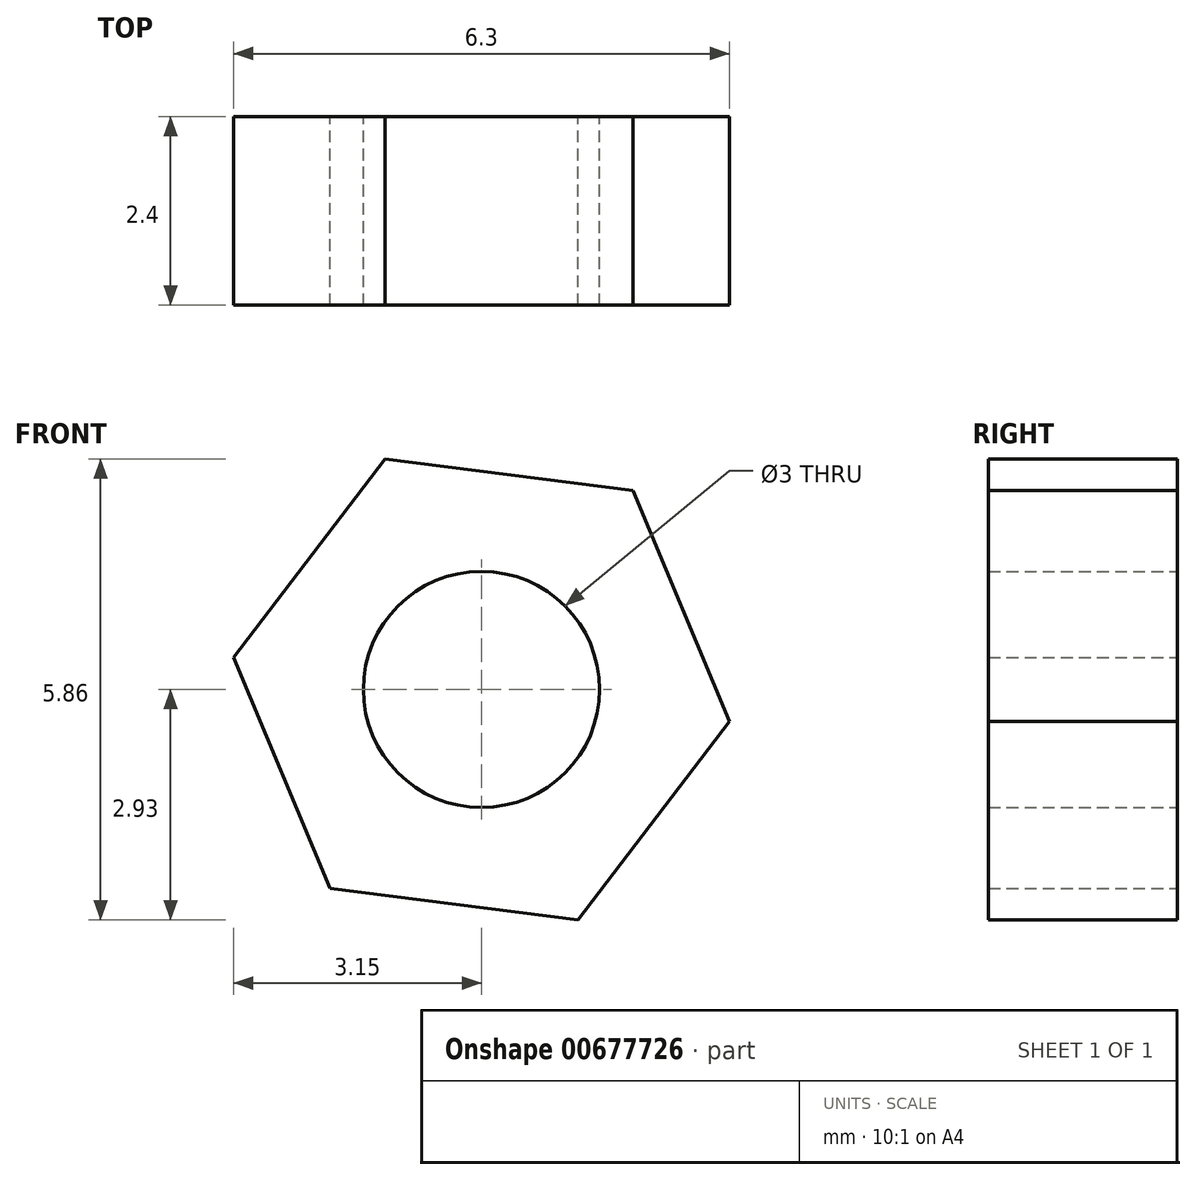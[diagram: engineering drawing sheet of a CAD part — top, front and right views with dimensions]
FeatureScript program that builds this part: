
annotation { "Feature Type Name" : "Feature", "Feature Type Description" : "" }
export const myFeature = defineFeature(function(context is Context, id is Id, definition is map)
    precondition{}
    {
        {
            var Q0;
            Q0=qCreatedBy(makeId("Front.planeOp"),FACE);
            var sketch = newSketch(context, id + "F0", { "sketchPlane" : qUnion([Q0])});
            skCircle(sketch, "E0.cCircle", {"center": v(0, 0) * mm, "radius": 2.75 * mm, "construction": true});
            skLineSegment(sketch, "E0.0", {"start": v(3.15, -0.4) * mm, "end": v(1.22, -2.93) * mm});
            skLineSegment(sketch, "E0.1", {"start": v(1.22, -2.93) * mm, "end": v(-1.93, -2.53) * mm});
            skLineSegment(sketch, "E0.2", {"start": v(-1.93, -2.53) * mm, "end": v(-3.15, 0.4) * mm});
            skLineSegment(sketch, "E0.3", {"start": v(-3.15, 0.4) * mm, "end": v(-1.22, 2.93) * mm});
            skLineSegment(sketch, "E0.4", {"start": v(-1.22, 2.93) * mm, "end": v(1.93, 2.53) * mm});
            skLineSegment(sketch, "E0.5", {"start": v(1.93, 2.53) * mm, "end": v(3.15, -0.4) * mm});
            skPoint(sketch, "E0.0.midPoint", {"position": v(2.19, -1.67) * mm});
            skCircle(sketch, "E1", {"center": v(0, 0) * mm, "radius": 1.5 * mm});
            skSolve(sketch);
        }
        {
            var Q0;
            Q0=makeQuery(id+"F0.imprint","IMPRINT",FACE,{"disambiguationData":[TD([[makeQuery(id+"F0.imprint","IMPRINT",EDGE,{"derivedFrom":sQuery(id+"F0.wireOp",EDGE,"E0.0")}),-1.0]])]});
            extrude(context, id + "F1", {"entities" : qUnion([Q0]), "depth" : 2.4 * mm, "offsetDistance" : 25.4 * mm});
        }
    });
